# Revit family: IS_Dea_T3316_BIM_DE
name_source: partatom
category: Plumbing Fixtures
revit_build: Autodesk Revit MEP 2016 (Build: 20161004_0715(x64)
units: mm (PartAtom-declared; Revit-internal decimal feet)

## family parameters
Cut with Voids When Loaded = No
Host = Face
OmniClass Number = 23.45.05.21.11.11
OmniClass Title = Water Operated Water Closets
Part Type = Normal
Room Calculation Point = No
Round Connector Dimension = Use Diameter
Shared = No

## types (4) — shared parameters
Accessories = www.idealstandard.de\ersatzteile
AreaUnits = millimeters
AssetType = Fixed
BIMobject category = Toilets
Brand = Ideal Standard
Brand url = http://www.idealstandard.co.uk
CodePerformance = DIN EN 997 CL1-5A/6A+CL2, DIN EN
ConnectionType = Plumbing
CurrencyUnit = €
Date of publishing = 5/15/2017
Default Elevation = 410 mm
DurationUnit = year
Edition number = 1
ExpectedLife = 25
Features = DEA wall mounted bowl 365x550mm, wash-down, rimless
GrossWeight = 24,3 kg
IFC Classification = Sanitary Terminal
Installation instructions = http://www.idealstandard.de
InstallationDate = 1900-12-31T23:59:59
InstallationInstructions = www.idealstandard.de\produkte
LinearUnits = millimeters
Manufacturer name = Ideal Standard
ManufacturerURL = www.idealstandard.de
Material = Vitreous china
Material main = Ceramics
NBS Reference Code = 35-93-94
NBS Reference Description = Wc Pans
Nominal height = 335 mm
Nominal width = 365 mm
NominalLength = 551 mm
Product Guid = d73e544f-a853-41d6-925f-439c77a580bc
Product SKU = T3316
Product data url = https://bimobject.com
Product family = DEA
Product group = Bowl
Product url = http://www.idealstandard.de
ProductInformation = www.idealstandard.de
QR code = http://bimobject.com
Technical description = http://www.idealstandard.de
URL = www.idealstandard.de
Uniclass 2.0 Code = PR-35-93-94
Uniclass 2.0 Description = Wc Pans
Uniclass 2015 Name = WC pans
Uniclass2015Code = Pr_40_20_93_94
Uniclass2015Title = WC pans
Uniclass2015Version = Products v1.1
Version = 1
Weight Net (Kg) = 23.3
zero-valued in all types: Cost, NominalDepth

## per-type parameters (varying)
| type | BIMObjectName | BarCode | Color | Description | EAN code | Finish | Model | ModelNumber | ModelReference | Name |
| T331601 - Inodoro suspendido DEA sin brida, blanco | ISI_IdealStandard_WCPans_DEA_T331601 | 8014140426677 | White | Inodoro suspendido DEA sin brida, blanco | https://8014140426677 | White | T331601 | T331601 | IS Wand-WC DEA, Spülrandlos, unsichtbare Bef., 365x550x335mm, Weiß | ISI_IdealStandard_WCPans_DEA_T331601 |
| T331683 - Inodoro suspendido DEA sin brida, blanco mate | ISI_IdealStandard_WCPans_DEA_T331683 | 8014140426684 | Matt White | Inodoro suspendido DEA sin brida, blanco mate | https://8014140426677 | Matt White | T331683 | T331683 | IS Wand-WC DEA, Spülrandlos, unsichtbare Bef., 365x550x335mm, Weiß seidenmatt | ISI_IdealStandard_WCPans_DEA_T331683 |
| T3316MI DEA wall mounted bowl 365x550mm, wash-down, rimless | ISI_IdealStandard_WCPans_DEA_T331601 | 8014140426738 | White | Inodoro suspendido DEA sin brida, blanco | https://8014140426738 | White | T3316MI | T331601 | IS Wand-WC DEA, Spülrandlos, unsichtbare Bef., 365x550x335mm, Weiß | ISI_IdealStandard_WCPans_DEA_T3316MI |
| T3316MA DEA wall mounted bowl 365x550mm, wash-down, rimless | ISI_IdealStandard_WCPans_DEA_T331601 | 8014140426721 | White | Inodoro suspendido DEA sin brida, blanco | https://8014140426721 | White | T3316MA | T331601 | IS Wand-WC DEA, Spülrandlos, unsichtbare Bef., 365x550x335mm, Weiß | ISI_IdealStandard_WCPans_DEA_T3316MA |

## geometry (parser evidence)
native form markers: Blend x4, Sweep x2
no freeform markers — native parametric forms only
